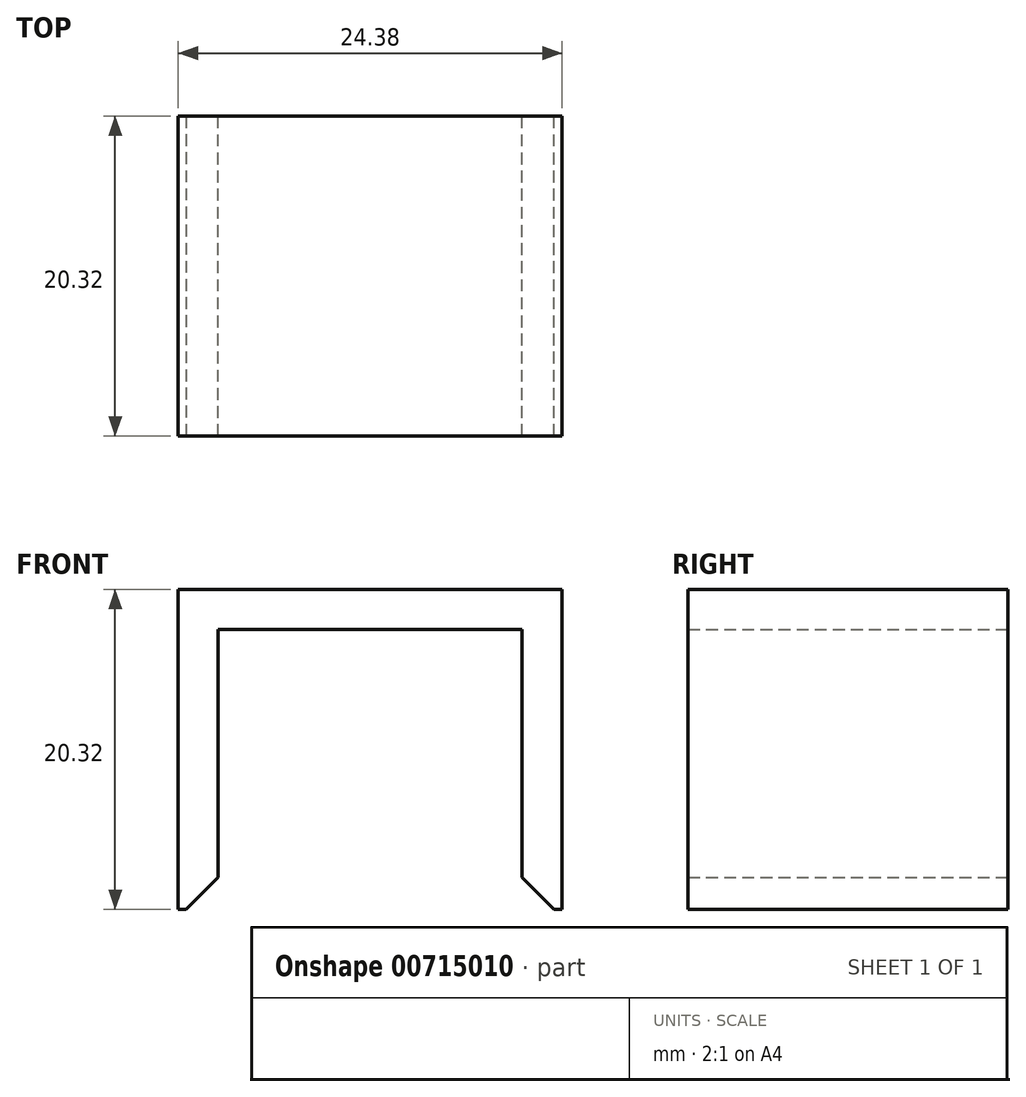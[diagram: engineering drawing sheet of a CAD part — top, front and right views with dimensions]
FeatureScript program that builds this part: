
annotation { "Feature Type Name" : "Feature", "Feature Type Description" : "" }
export const myFeature = defineFeature(function(context is Context, id is Id, definition is map)
    precondition{}
    {
        {
            var Q0;
            Q0=qCreatedBy(makeId("Front.planeOp"),FACE);
            var sketch = newSketch(context, id + "F0", { "sketchPlane" : qUnion([Q0])});
            skLineSegment(sketch, "E0.bottom", {"start": v(-12.2, 10.16) * mm, "end": v(12.2, 10.16) * mm});
            skLineSegment(sketch, "E0.top", {"start": v(-12.2, -10.16) * mm, "end": v(-9.65, -10.16) * mm});
            skLineSegment(sketch, "E0.left", {"start": v(-12.2, 10.16) * mm, "end": v(-12.2, -10.16) * mm});
            skLineSegment(sketch, "E0.right", {"start": v(12.2, 10.16) * mm, "end": v(12.2, -10.16) * mm});
            skPoint(sketch, "E0.middle", {"position": v(0, 0) * mm});
            skLineSegment(sketch, "E1.top", {"start": v(-9.65, 7.62) * mm, "end": v(9.65, 7.62) * mm});
            skLineSegment(sketch, "E1.left", {"start": v(-9.65, -7.62) * mm, "end": v(-9.65, 7.62) * mm});
            skLineSegment(sketch, "E1.right", {"start": v(9.65, -7.62) * mm, "end": v(9.65, 7.62) * mm});
            skLineSegment(sketch, "E2", {"start": v(-9.65, -7.62) * mm, "end": v(-9.65, -10.16) * mm});
            skLineSegment(sketch, "E3", {"start": v(9.65, -7.62) * mm, "end": v(9.65, -10.16) * mm});
            skLineSegment(sketch, "E4.trimOffspring", {"start": v(9.65, -10.16) * mm, "end": v(12.2, -10.16) * mm});
            skSolve(sketch);
        }
        {
            var Q0;
            Q0=makeQuery(id+"F0.imprint","IMPRINT",FACE,{"disambiguationData":[TD([[makeQuery(id+"F0.imprint","IMPRINT",EDGE,{"derivedFrom":sQuery(id+"F0.wireOp",EDGE,"E0.bottom")}),-1.0]])]});
            extrude(context, id + "F1", {"entities" : qUnion([Q0]), "depth" : 20.32 * mm, "offsetDistance" : 25.4 * mm});
        }
        {
            var Q0;
            Q0=makeQuery(id+"F1.opExtrude","SWEPT_EDGE",EDGE,{"disambiguationData":[OSD([sQuery(id+"F0.wireOp",EDGE,"E0.top"),sQuery(id+"F0.wireOp",EDGE,"E2")])]});
            var Q1;
            Q1=makeQuery(id+"F1.opExtrude","SWEPT_EDGE",EDGE,{"disambiguationData":[OSD([sQuery(id+"F0.wireOp",EDGE,"E3"),sQuery(id+"F0.wireOp",EDGE,"E4.trimOffspring")])]});
            chamfer(context, id + "F2", {"entities" : qUnion([Q0, Q1]), "width" : 2.03 * mm, "tangentPropagation" : true});
        }
    });
